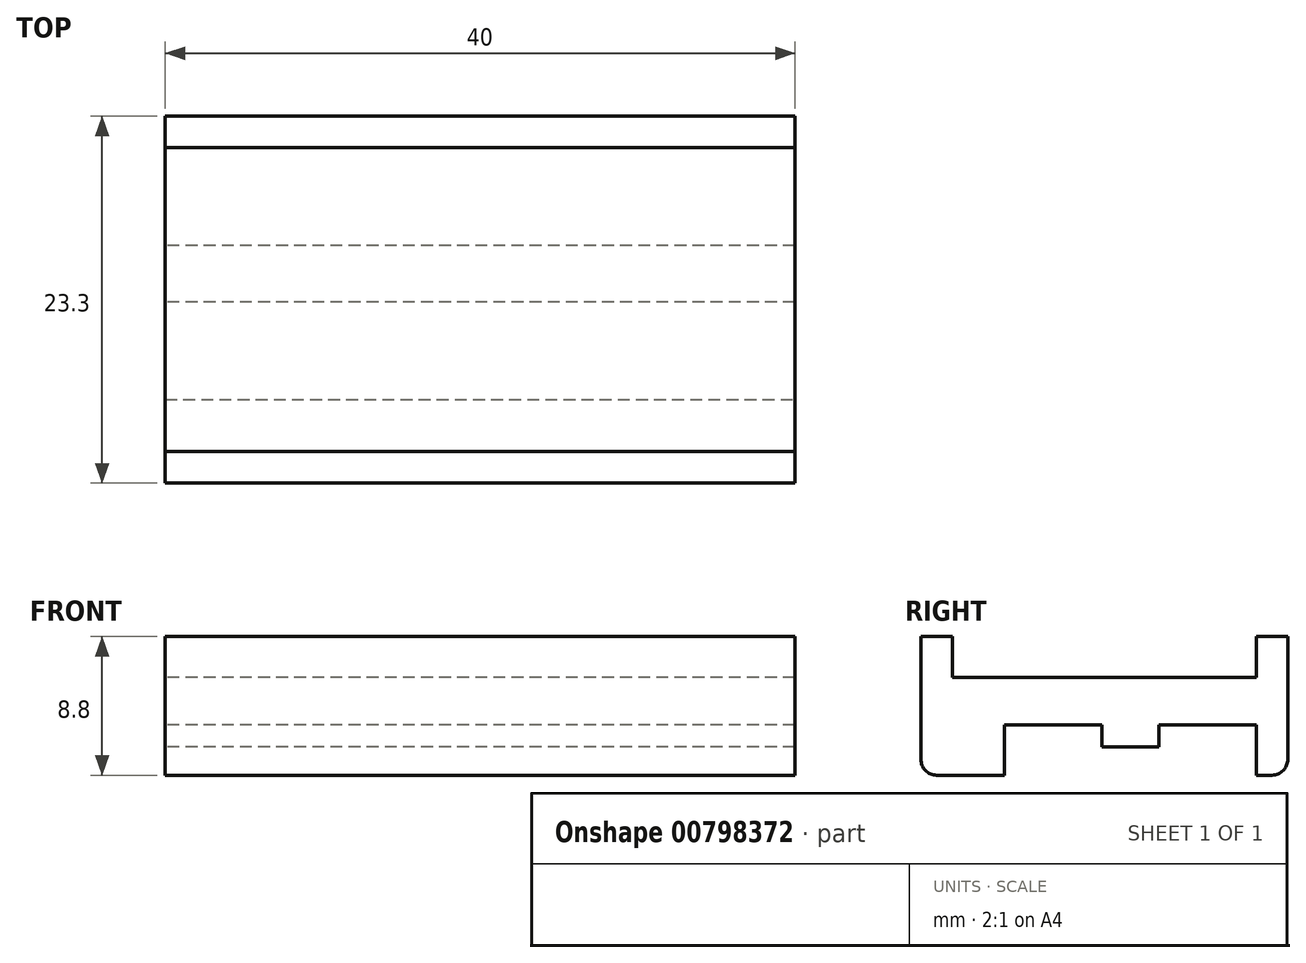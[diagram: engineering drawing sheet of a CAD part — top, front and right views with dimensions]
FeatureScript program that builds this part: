
annotation { "Feature Type Name" : "Feature", "Feature Type Description" : "" }
export const myFeature = defineFeature(function(context is Context, id is Id, definition is map)
    precondition{}
    {
        {
            var Q0;
            Q0=qCreatedBy(makeId("Top.planeOp"),FACE);
            var sketch = newSketch(context, id + "F0", { "sketchPlane" : qUnion([Q0])});
            skLineSegment(sketch, "E0.bottom", {"start": v(0, 0) * mm, "end": v(40, 0) * mm});
            skLineSegment(sketch, "E0.top", {"start": v(0, -23.3) * mm, "end": v(40, -23.3) * mm});
            skLineSegment(sketch, "E0.left", {"start": v(0, 0) * mm, "end": v(0, -23.3) * mm});
            skLineSegment(sketch, "E0.right", {"start": v(40, 0) * mm, "end": v(40, -23.3) * mm});
            skLineSegment(sketch, "E1.top", {"start": v(0, -2) * mm, "end": v(40, -2) * mm});
            skLineSegment(sketch, "E1.left", {"start": v(0, 0) * mm, "end": v(0, -2) * mm});
            skLineSegment(sketch, "E1.right", {"start": v(40, 0) * mm, "end": v(40, -2) * mm});
            skLineSegment(sketch, "E2.top", {"start": v(0, -21.3) * mm, "end": v(40, -21.3) * mm});
            skLineSegment(sketch, "E2.left", {"start": v(0, -23.3) * mm, "end": v(0, -21.3) * mm});
            skLineSegment(sketch, "E2.right", {"start": v(40, -23.3) * mm, "end": v(40, -21.3) * mm});
            skSolve(sketch);
        }
        {
            var Q0;
            Q0=makeQuery(id+"F0.imprint","IMPRINT",FACE,{"disambiguationData":[TD([[makeQuery(id+"F0.imprint","IMPRINT",EDGE,{"derivedFrom":sQuery(id+"F0.wireOp",EDGE,"E0.left")}),1.0]])]});
            extrude(context, id + "F1", {"entities" : qUnion([Q0]), "depth" : 3 * mm, "offsetDistance" : 25 * mm});
        }
        {
            var Q0;
            Q0=makeQuery(id+"F0.imprint","IMPRINT",FACE,{"disambiguationData":[TD([[makeQuery(id+"F0.imprint","IMPRINT",EDGE,{"derivedFrom":sQuery(id+"F0.wireOp",EDGE,"E0.top")}),1.0]])]});
            var Q1;
            Q1=makeQuery(id+"F0.imprint","IMPRINT",FACE,{"disambiguationData":[TD([[makeQuery(id+"F0.imprint","IMPRINT",EDGE,{"derivedFrom":sQuery(id+"F0.wireOp",EDGE,"E0.bottom")}),-1.0]])]});
            extrude(context, id + "F2", {"entities" : qUnion([Q0, Q1]), "operationType" : NewBodyOperationType.ADD, "depth" : 5.6 * mm, "offsetDistance" : 25 * mm});
        }
        {
            var Q0;
            Q0=qCreatedBy(makeId("Top.planeOp"),FACE);
            var sketch = newSketch(context, id + "F3", { "sketchPlane" : qUnion([Q0])});
            skLineSegment(sketch, "E3.bottom", {"start": v(0, 0) * mm, "end": v(40, 0) * mm});
            skLineSegment(sketch, "E3.top", {"start": v(0, -2) * mm, "end": v(40, -2) * mm});
            skLineSegment(sketch, "E3.left", {"start": v(0, 0) * mm, "end": v(0, -2) * mm});
            skLineSegment(sketch, "E3.right", {"start": v(40, 0) * mm, "end": v(40, -2) * mm});
            skLineSegment(sketch, "E4.bottom", {"start": v(0, -23.3) * mm, "end": v(40, -23.3) * mm});
            skLineSegment(sketch, "E4.top", {"start": v(0, -18) * mm, "end": v(40, -18) * mm});
            skLineSegment(sketch, "E4.left", {"start": v(0, -23.3) * mm, "end": v(0, -18) * mm});
            skLineSegment(sketch, "E4.right", {"start": v(40, -23.3) * mm, "end": v(40, -18) * mm});
            skPoint(sketch, "E5", {"position": v(40, -10) * mm});
            skLineSegment(sketch, "E6", {"start": v(40, -10) * mm, "end": v(0, -10) * mm});
            skLineSegment(sketch, "E7.top", {"start": v(40, -8.2) * mm, "end": v(0, -8.2) * mm});
            skLineSegment(sketch, "E7.left", {"start": v(40, -10) * mm, "end": v(40, -8.2) * mm});
            skLineSegment(sketch, "E7.right", {"start": v(0, -10) * mm, "end": v(0, -8.2) * mm});
            skLineSegment(sketch, "E8.MirrorCS", {"start": v(40, -11.8) * mm, "end": v(0, -11.8) * mm});
            skLineSegment(sketch, "E9.MirrorCS", {"start": v(40, -10) * mm, "end": v(40, -11.8) * mm});
            skLineSegment(sketch, "E10.MirrorCS", {"start": v(0, -10) * mm, "end": v(0, -11.8) * mm});
            skSolve(sketch);
        }
        {
            var Q0;
            Q0=makeQuery(id+"F0.imprint","IMPRINT",FACE,{"disambiguationData":[TD([[makeQuery(id+"F0.imprint","IMPRINT",EDGE,{"derivedFrom":sQuery(id+"F0.wireOp",EDGE,"E0.bottom")}),-1.0]])]});
            var Q1;
            Q1=makeQuery(id+"F3.imprint","IMPRINT",FACE,{"disambiguationData":[TD([[makeQuery(id+"F3.imprint","IMPRINT",EDGE,{"derivedFrom":sQuery(id+"F3.wireOp",EDGE,"E4.bottom")}),1.0]])]});
            extrude(context, id + "F4", {"entities" : qUnion([Q0, Q1]), "operationType" : NewBodyOperationType.ADD, "oppositeDirection" : true, "depth" : 3.2 * mm, "offsetDistance" : 25 * mm});
        }
        {
            var Q0;
            Q0=makeQuery(id+"F4.opExtrude","CAP_EDGE",EDGE,{"disambiguationData":[OSD([sQuery(id+"F3.wireOp",EDGE,"E4.bottom")])],"isStart":false});
            var Q1;
            Q1=makeQuery(id+"F4.opExtrude","CAP_EDGE",EDGE,{"disambiguationData":[OSD([sQuery(id+"F0.wireOp",EDGE,"E0.bottom")])],"isStart":false});
            fillet(context, id + "F5", {"entities" : qUnion([Q0, Q1]), "radius" : 1 * mm, "tangentPropagation" : true, "allowEdgeOverflow" : false});
        }
        {
            var Q0;
            Q0=makeQuery(id+"F3.imprint","IMPRINT",FACE,{"disambiguationData":[TD([[makeQuery(id+"F3.imprint","IMPRINT",EDGE,{"derivedFrom":sQuery(id+"F3.wireOp",EDGE,"E6")}),-1.0]])]});
            var Q1;
            Q1=makeQuery(id+"F3.imprint","IMPRINT",FACE,{"disambiguationData":[TD([[makeQuery(id+"F3.imprint","IMPRINT",EDGE,{"derivedFrom":sQuery(id+"F3.wireOp",EDGE,"E6")}),1.0]])]});
            extrude(context, id + "F6", {"entities" : qUnion([Q0, Q1]), "operationType" : NewBodyOperationType.ADD, "oppositeDirection" : true, "depth" : 1.4 * mm, "offsetDistance" : 25 * mm});
        }
    });
